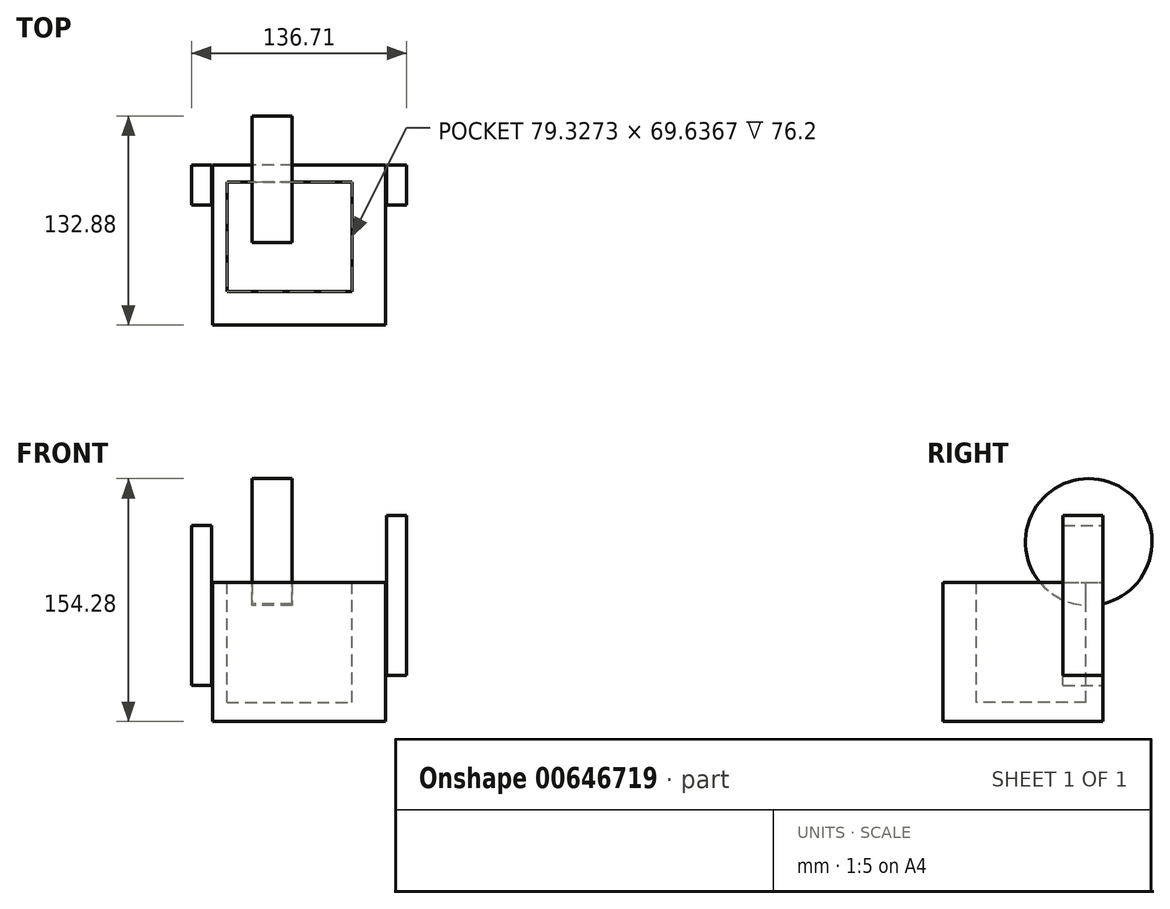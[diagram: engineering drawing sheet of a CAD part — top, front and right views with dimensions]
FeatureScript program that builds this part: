
annotation { "Feature Type Name" : "Feature", "Feature Type Description" : "" }
export const myFeature = defineFeature(function(context is Context, id is Id, definition is map)
    precondition{}
    {
        {
            var Q0;
            Q0=qCreatedBy(makeId("Front.planeOp"),FACE);
            var sketch = newSketch(context, id + "F0", { "sketchPlane" : qUnion([Q0])});
            skLineSegment(sketch, "E0.bottom", {"start": v(-25.04, 8.8) * mm, "end": v(84.73, 8.8) * mm});
            skLineSegment(sketch, "E0.top", {"start": v(-25.04, -79.51) * mm, "end": v(84.73, -79.51) * mm});
            skLineSegment(sketch, "E0.left", {"start": v(-25.04, 8.8) * mm, "end": v(-25.04, -79.51) * mm});
            skLineSegment(sketch, "E0.right", {"start": v(84.73, 8.8) * mm, "end": v(84.73, -79.51) * mm});
            skSolve(sketch);
        }
        {
            var Q0;
            Q0=makeQuery(id+"F0.imprint","IMPRINT",FACE,{"disambiguationData":[TD([[makeQuery(id+"F0.imprint","IMPRINT",EDGE,{"derivedFrom":sQuery(id+"F0.wireOp",EDGE,"E0.bottom")}),-1.0]])]});
            extrude(context, id + "F1", {"entities" : qUnion([Q0]), "depth" : 101.6 * mm, "offsetDistance" : 25.4 * mm});
        }
        {
            var Q0;
            Q0=makeQuery(id+"F1.opExtrude","SWEPT_FACE",FACE,{"disambiguationData":[OSD([sQuery(id+"F0.wireOp",EDGE,"E0.bottom")])]});
            var sketch = newSketch(context, id + "F2", { "sketchPlane" : qUnion([Q0])});
            skLineSegment(sketch, "E1", {"start": v(-16.04, -10.7) * mm, "end": v(-16.04, -80.34) * mm});
            skLineSegment(sketch, "E2", {"start": v(-16.04, -80.34) * mm, "end": v(63.29, -80.34) * mm});
            skLineSegment(sketch, "E3", {"start": v(63.29, -80.34) * mm, "end": v(63.29, -18.58) * mm});
            skLineSegment(sketch, "E4", {"start": v(-16.04, -10.7) * mm, "end": v(63.29, -10.7) * mm});
            skLineSegment(sketch, "E5", {"start": v(63.29, -10.7) * mm, "end": v(63.29, -18.58) * mm});
            skSolve(sketch);
        }
        {
            var Q0;
            Q0=makeQuery(id+"F2.imprint","IMPRINT",FACE,{"disambiguationData":[TD([[makeQuery(id+"F2.imprint","IMPRINT",EDGE,{"derivedFrom":sQuery(id+"F2.wireOp",EDGE,"E1")}),1.0]])]});
            extrude(context, id + "F3", {"entities" : qUnion([Q0]), "operationType" : NewBodyOperationType.REMOVE, "oppositeDirection" : true, "depth" : 76.2 * mm, "offsetDistance" : 25.4 * mm});
        }
        {
            var Q0;
            Q0=qCreatedBy(makeId("Front.planeOp"),FACE);
            var sketch = newSketch(context, id + "F4", { "sketchPlane" : qUnion([Q0])});
            skLineSegment(sketch, "E6", {"start": v(-25.95, -56.54) * mm, "end": v(-25.95, 45.06) * mm});
            skLineSegment(sketch, "E7", {"start": v(-25.95, 45.06) * mm, "end": v(-38.65, 45.06) * mm});
            skLineSegment(sketch, "E8", {"start": v(-38.65, 45.06) * mm, "end": v(-38.65, -56.54) * mm});
            skLineSegment(sketch, "E9", {"start": v(-38.65, -56.54) * mm, "end": v(-25.95, -56.54) * mm});
            skLineSegment(sketch, "E10", {"start": v(85.36, -50.06) * mm, "end": v(85.36, 51.54) * mm});
            skLineSegment(sketch, "E11", {"start": v(85.36, 51.54) * mm, "end": v(98.06, 51.54) * mm});
            skLineSegment(sketch, "E12", {"start": v(98.06, 51.54) * mm, "end": v(98.06, -50.06) * mm});
            skLineSegment(sketch, "E13", {"start": v(98.06, -50.06) * mm, "end": v(85.36, -50.06) * mm});
            skSolve(sketch);
        }
        {
            var Q0;
            Q0=makeQuery(id+"F4.imprint","IMPRINT",FACE,{"disambiguationData":[TD([[makeQuery(id+"F4.imprint","IMPRINT",EDGE,{"derivedFrom":sQuery(id+"F4.wireOp",EDGE,"E6")}),1.0]])]});
            var Q1;
            Q1=makeQuery(id+"F4.imprint","IMPRINT",FACE,{"disambiguationData":[TD([[makeQuery(id+"F4.imprint","IMPRINT",EDGE,{"derivedFrom":sQuery(id+"F4.wireOp",EDGE,"E10")}),-1.0]])]});
            extrude(context, id + "F5", {"entities" : qUnion([Q0, Q1]), "depth" : 25.4 * mm, "offsetDistance" : 25.4 * mm});
        }
        {
            var Q0;
            Q0=qCreatedBy(makeId("Right.planeOp"),FACE);
            var sketch = newSketch(context, id + "F6", { "sketchPlane" : qUnion([Q0])});
            skCircle(sketch, "E14", {"center": v(-8.94, 34.55) * mm, "radius": 40.22 * mm});
            skSolve(sketch);
        }
        {
            var Q0;
            Q0=makeQuery(id+"F6.imprint","IMPRINT",FACE,{"disambiguationData":[TD([[makeQuery(id+"F6.imprint","IMPRINT",EDGE,{"derivedFrom":sQuery(id+"F6.wireOp",EDGE,"E14")}),1.0]])]});
            extrude(context, id + "F7", {"entities" : qUnion([Q0]), "operationType" : NewBodyOperationType.ADD, "depth" : 25.4 * mm, "offsetDistance" : 25.4 * mm});
        }
    });
